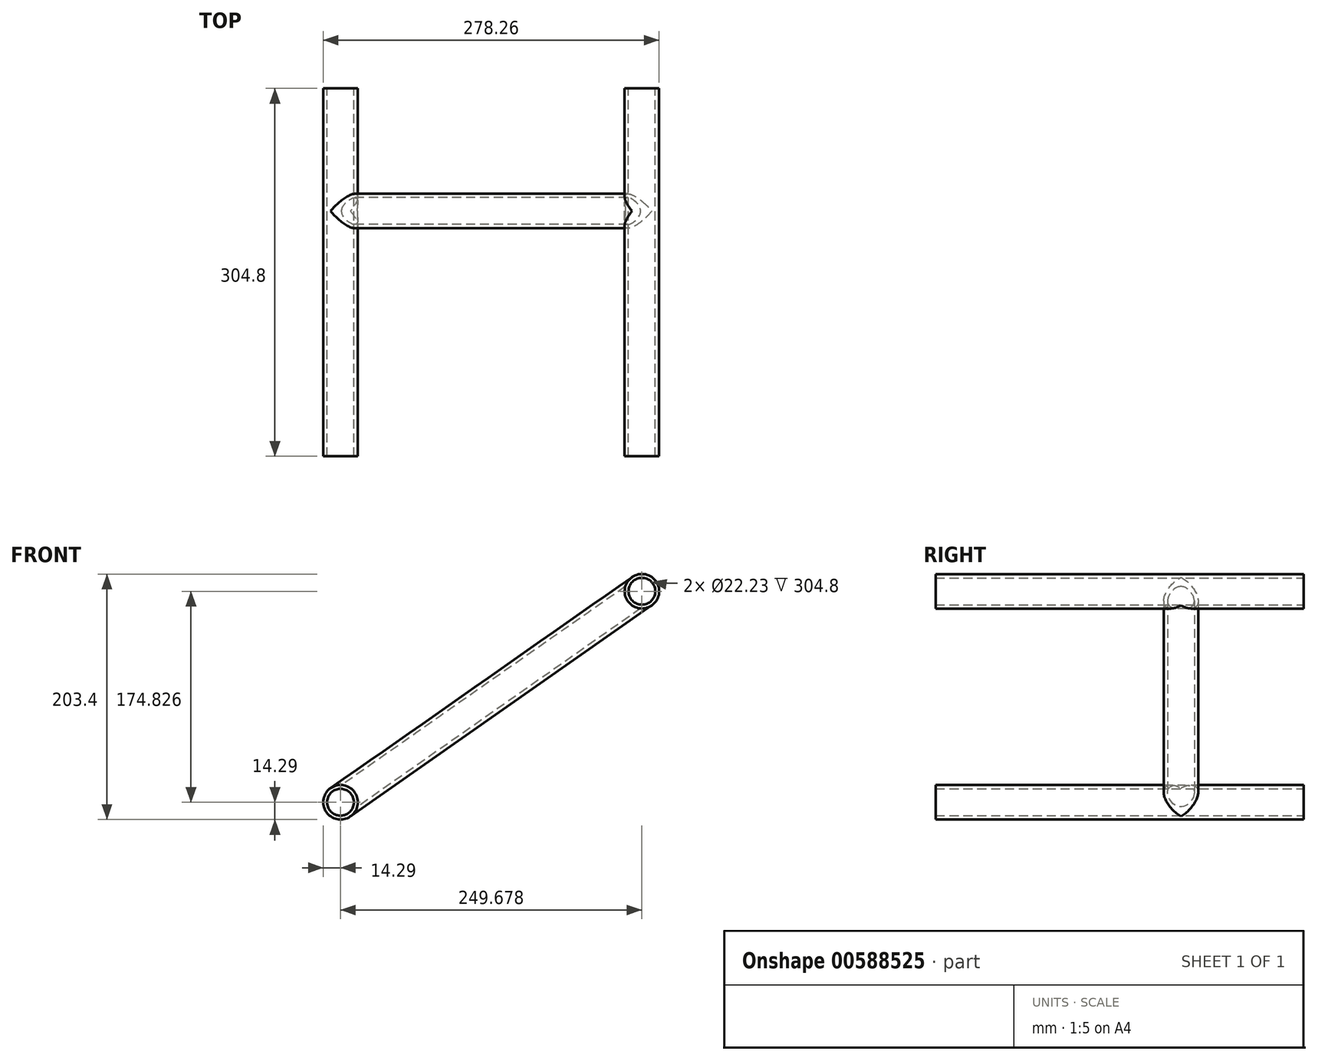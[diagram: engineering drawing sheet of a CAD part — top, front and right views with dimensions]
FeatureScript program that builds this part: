
annotation { "Feature Type Name" : "Feature", "Feature Type Description" : "" }
export const myFeature = defineFeature(function(context is Context, id is Id, definition is map)
    precondition{}
    {
        {
            var Q0;
            Q0=qCreatedBy(makeId("Front.planeOp"),FACE);
            var sketch = newSketch(context, id + "F0", { "sketchPlane" : qUnion([Q0])});
            skLineSegment(sketch, "E0", {"start": v(0, 0) * mm, "end": v(128.09, 0) * mm, "construction": true});
            skLineSegment(sketch, "E1", {"start": v(0, 0) * mm, "end": v(249.68, 174.83) * mm, "construction": true});
            skCircle(sketch, "E2", {"center": v(0, 0) * mm, "radius": 14.29 * mm});
            skCircle(sketch, "E3.0", {"center": v(0, 0) * mm, "radius": 11.11 * mm});
            skCircle(sketch, "E4", {"center": v(249.68, 174.83) * mm, "radius": 14.29 * mm});
            skCircle(sketch, "E5.0", {"center": v(249.68, 174.83) * mm, "radius": 11.11 * mm});
            skSolve(sketch);
        }
        {
            var Q0;
            Q0=makeQuery(id+"F0.imprint","IMPRINT",FACE,{"disambiguationData":[TD([[makeQuery(id+"F0.imprint","IMPRINT",EDGE,{"derivedFrom":sQuery(id+"F0.wireOp",EDGE,"E2")}),1.0]])]});
            var Q1;
            Q1=makeQuery(id+"F0.imprint","IMPRINT",FACE,{"disambiguationData":[TD([[makeQuery(id+"F0.imprint","IMPRINT",EDGE,{"derivedFrom":sQuery(id+"F0.wireOp",EDGE,"E4")}),1.0]])]});
            extrude(context, id + "F1", {"entities" : qUnion([Q0, Q1]), "endBound" : BoundingType.SYMMETRIC, "depth" : 304.8 * mm, "offsetDistance" : 25.4 * mm});
        }
        {
            var Q0;
            Q0=sQuery(id+"F0.wireOp",EDGE,"E1");
            cPlane(context, id + "F2", {"entities" : qUnion([Q0]), "cplaneType" : CPlaneType.MID_PLANE, "offset" : 25.4 * mm, "width" : 152.4 * mm, "height" : 152.4 * mm});
        }
        {
            var Q0;
            Q0=qCreatedBy(id+"F2.planeOp",FACE);
            var sketch = newSketch(context, id + "F3", { "sketchPlane" : qUnion([Q0])});
            skCircle(sketch, "E6", {"center": v(50.8, 0) * mm, "radius": 14.29 * mm});
            skCircle(sketch, "E7.0", {"center": v(50.8, 0) * mm, "radius": 11.11 * mm});
            skCircle(sketch, "E8.MirrorC", {"center": v(-50.8, 0) * mm, "radius": 14.29 * mm});
            skCircle(sketch, "E9.MirrorC", {"center": v(-50.8, 0) * mm, "radius": 11.11 * mm});
            skSolve(sketch);
        }
        {
            var Q0;
            Q0=makeQuery(id+"F3.imprint","IMPRINT",FACE,{"disambiguationData":[TD([[makeQuery(id+"F3.imprint","IMPRINT",EDGE,{"derivedFrom":sQuery(id+"F3.wireOp",EDGE,"E8.MirrorC")}),-1.0]])]});
            var Q1;
            Q1=makeQuery(id+"F3.imprint","IMPRINT",FACE,{"disambiguationData":[TD([[makeQuery(id+"F3.imprint","IMPRINT",EDGE,{"derivedFrom":sQuery(id+"F3.wireOp",EDGE,"E6")}),1.0]])]});
            extrude(context, id + "F4", {"entities" : qUnion([Q0, Q1]), "operationType" : NewBodyOperationType.ADD, "endBound" : BoundingType.UP_TO_NEXT, "depth" : 25.4 * mm, "offsetDistance" : 25.4 * mm, "hasSecondDirection" : true, "secondDirectionBound" : SecondDirectionBoundingType.UP_TO_NEXT, "secondDirectionOppositeDirection" : true, "secondDirectionDepth" : 25.4 * mm});
        }
    });
